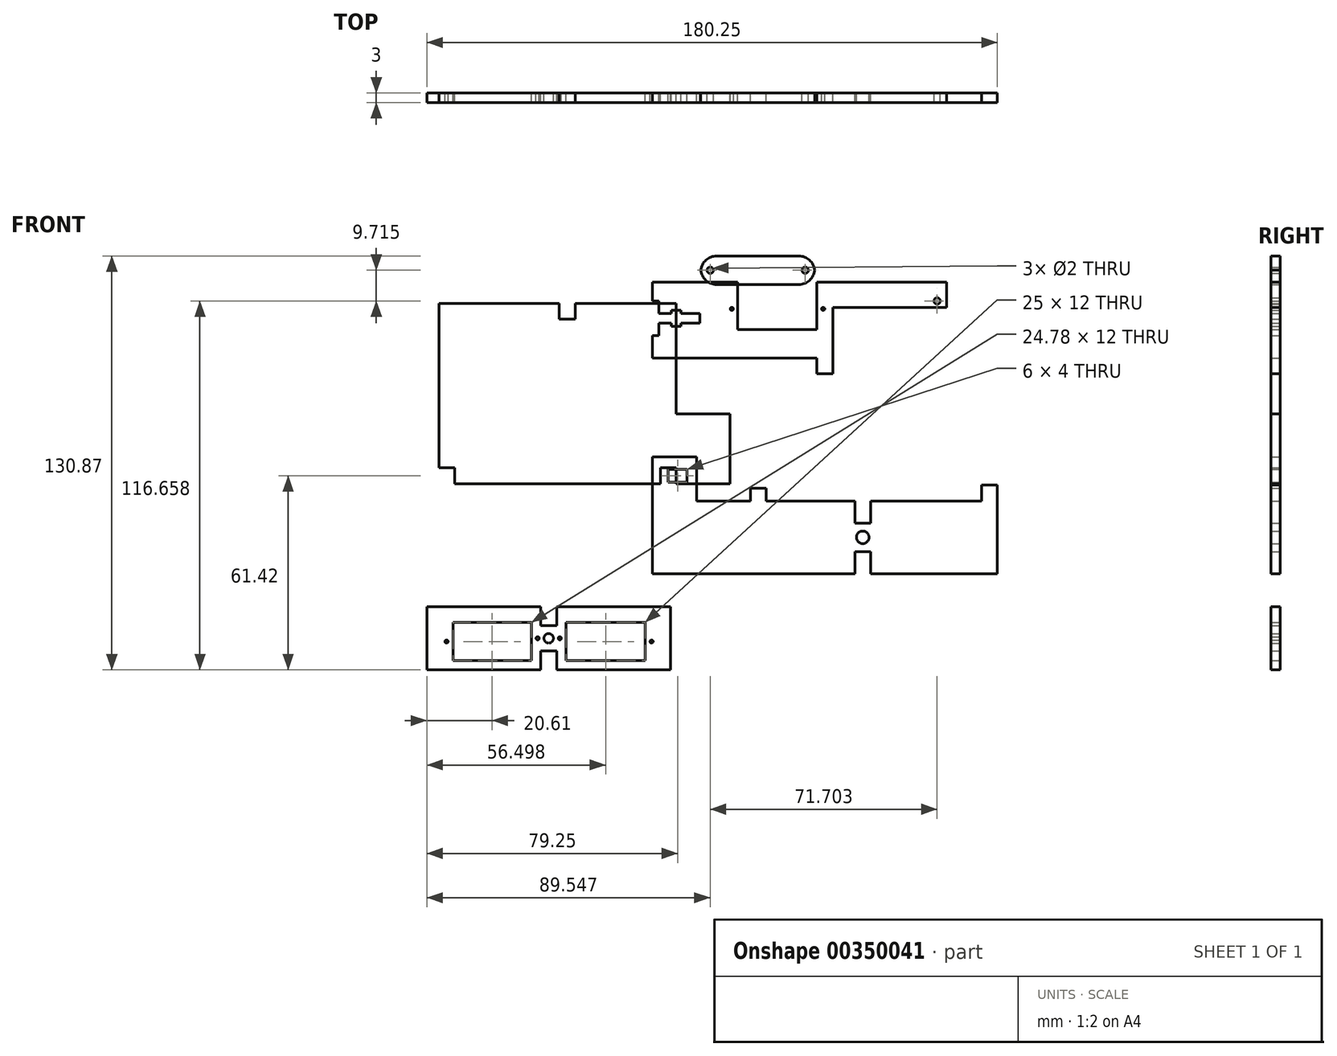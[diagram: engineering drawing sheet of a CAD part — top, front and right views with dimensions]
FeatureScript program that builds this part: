
annotation { "Feature Type Name" : "Feature", "Feature Type Description" : "" }
export const myFeature = defineFeature(function(context is Context, id is Id, definition is map)
    precondition{}
    {
        {
            var Q0;
            Q0=qCreatedBy(makeId("Front.planeOp"),FACE);
            var sketch = newSketch(context, id + "F0", { "sketchPlane" : qUnion([Q0])});
            skLineSegment(sketch, "E0", {"start": v(-67.42, 48.47) * mm, "end": v(-29.42, 48.47) * mm});
            skLineSegment(sketch, "E1", {"start": v(-29.42, 48.47) * mm, "end": v(-29.42, 43.47) * mm});
            skLineSegment(sketch, "E2", {"start": v(-29.42, 43.47) * mm, "end": v(-24.42, 43.47) * mm});
            skLineSegment(sketch, "E3", {"start": v(-24.42, 43.47) * mm, "end": v(-24.42, 48.47) * mm});
            skLineSegment(sketch, "E4", {"start": v(-24.42, 48.47) * mm, "end": v(7.58, 48.47) * mm});
            skLineSegment(sketch, "E5", {"start": v(7.58, 48.47) * mm, "end": v(7.58, 13.47) * mm});
            skLineSegment(sketch, "E6", {"start": v(7.58, 13.47) * mm, "end": v(24.58, 13.47) * mm});
            skLineSegment(sketch, "E7", {"start": v(24.58, 13.47) * mm, "end": v(24.58, -8.53) * mm});
            skLineSegment(sketch, "E8", {"start": v(24.58, -8.53) * mm, "end": v(7.58, -8.53) * mm});
            skLineSegment(sketch, "E9", {"start": v(7.58, -8.53) * mm, "end": v(7.58, -3.53) * mm});
            skLineSegment(sketch, "E10", {"start": v(7.58, -3.53) * mm, "end": v(2.58, -3.53) * mm});
            skLineSegment(sketch, "E11", {"start": v(2.58, -3.53) * mm, "end": v(2.58, -8.53) * mm});
            skLineSegment(sketch, "E12", {"start": v(2.58, -8.53) * mm, "end": v(-62.42, -8.53) * mm});
            skLineSegment(sketch, "E13", {"start": v(-62.42, -8.53) * mm, "end": v(-62.42, -3.53) * mm});
            skLineSegment(sketch, "E14", {"start": v(-62.42, -3.53) * mm, "end": v(-67.42, -3.53) * mm});
            skLineSegment(sketch, "E15", {"start": v(-67.42, 48.47) * mm, "end": v(-67.42, -3.53) * mm});
            skSolve(sketch);
        }
        {
            var Q0;
            Q0 = qSketchRegion(id + "F0", true);
            extrude(context, id + "F1", {"entities" : qUnion([Q0]), "depth" : 3 * mm});
        }
        {
            var Q0;
            Q0=qCreatedBy(makeId("Front.planeOp"),FACE);
            var sketch = newSketch(context, id + "F2", { "sketchPlane" : qUnion([Q0])});
            skLineSegment(sketch, "E16", {"start": v(0, 0) * mm, "end": v(14, 0) * mm});
            skLineSegment(sketch, "E17", {"start": v(14, 0) * mm, "end": v(14, -14) * mm});
            skLineSegment(sketch, "E18", {"start": v(14, -14) * mm, "end": v(31, -14) * mm});
            skLineSegment(sketch, "E19", {"start": v(31, -14) * mm, "end": v(31, -10) * mm});
            skLineSegment(sketch, "E20", {"start": v(31, -10) * mm, "end": v(36, -10) * mm});
            skLineSegment(sketch, "E21", {"start": v(36, -10) * mm, "end": v(36, -14) * mm});
            skLineSegment(sketch, "E22", {"start": v(36, -14) * mm, "end": v(64, -14) * mm});
            skLineSegment(sketch, "E23", {"start": v(64, -14) * mm, "end": v(64, -21) * mm});
            skLineSegment(sketch, "E24", {"start": v(64, -21) * mm, "end": v(69, -21) * mm});
            skLineSegment(sketch, "E25", {"start": v(69, -21) * mm, "end": v(69, -14) * mm});
            skLineSegment(sketch, "E26", {"start": v(69, -14) * mm, "end": v(104, -14) * mm});
            skLineSegment(sketch, "E27", {"start": v(104, -14) * mm, "end": v(104, -9) * mm});
            skLineSegment(sketch, "E28", {"start": v(104, -9) * mm, "end": v(109, -9) * mm});
            skLineSegment(sketch, "E29", {"start": v(109, -9) * mm, "end": v(109, -37) * mm});
            skLineSegment(sketch, "E30", {"start": v(109, -37) * mm, "end": v(69, -37) * mm});
            skLineSegment(sketch, "E31", {"start": v(69, -37) * mm, "end": v(69, -30) * mm});
            skLineSegment(sketch, "E32", {"start": v(69, -30) * mm, "end": v(64, -30) * mm});
            skLineSegment(sketch, "E33", {"start": v(64, -30) * mm, "end": v(64, -37) * mm});
            skLineSegment(sketch, "E34", {"start": v(64, -37) * mm, "end": v(0, -37) * mm});
            skLineSegment(sketch, "E35", {"start": v(0, -37) * mm, "end": v(0, 0) * mm});
            skCircle(sketch, "E36", {"center": v(66.5, -25.5) * mm, "radius": 2 * mm});
            skLineSegment(sketch, "E37.bottom", {"start": v(5, -4) * mm, "end": v(11, -4) * mm});
            skLineSegment(sketch, "E37.top", {"start": v(5, -8) * mm, "end": v(11, -8) * mm});
            skLineSegment(sketch, "E37.left", {"start": v(5, -4) * mm, "end": v(5, -8) * mm});
            skLineSegment(sketch, "E37.right", {"start": v(11, -4) * mm, "end": v(11, -8) * mm});
            skSolve(sketch);
        }
        {
            var Q0;
            Q0 = qSketchRegion(id + "F2", true);
            extrude(context, id + "F3", {"entities" : qUnion([Q0]), "depth" : 3 * mm});
        }
        {
            var Q0;
            Q0=qCreatedBy(makeId("Front.planeOp"),FACE);
            var sketch = newSketch(context, id + "F4", { "sketchPlane" : qUnion([Q0])});
            skLineSegment(sketch, "E38", {"start": v(-71.25, -67.42) * mm, "end": v(-35.25, -67.42) * mm});
            skLineSegment(sketch, "E39", {"start": v(-35.25, -67.42) * mm, "end": v(-35.25, -61.42) * mm});
            skLineSegment(sketch, "E40", {"start": v(-35.25, -61.42) * mm, "end": v(-30.25, -61.42) * mm});
            skLineSegment(sketch, "E41", {"start": v(-30.25, -61.42) * mm, "end": v(-30.25, -67.42) * mm});
            skLineSegment(sketch, "E42", {"start": v(-30.25, -67.42) * mm, "end": v(5.75, -67.42) * mm});
            skLineSegment(sketch, "E43", {"start": v(5.75, -67.42) * mm, "end": v(5.75, -47.42) * mm});
            skLineSegment(sketch, "E44", {"start": v(5.75, -47.42) * mm, "end": v(-30.25, -47.42) * mm});
            skLineSegment(sketch, "E45", {"start": v(-30.25, -47.42) * mm, "end": v(-30.25, -53.42) * mm});
            skLineSegment(sketch, "E46", {"start": v(-30.25, -53.42) * mm, "end": v(-35.25, -53.42) * mm});
            skLineSegment(sketch, "E47", {"start": v(-35.25, -53.42) * mm, "end": v(-35.25, -47.42) * mm});
            skLineSegment(sketch, "E48", {"start": v(-35.25, -47.42) * mm, "end": v(-71.25, -47.42) * mm});
            skLineSegment(sketch, "E49", {"start": v(-71.25, -47.42) * mm, "end": v(-71.25, -67.42) * mm});
            skLineSegment(sketch, "E50.bottom", {"start": v(-63.03, -52.42) * mm, "end": v(-38.25, -52.42) * mm});
            skLineSegment(sketch, "E50.top", {"start": v(-63.03, -64.42) * mm, "end": v(-38.25, -64.42) * mm});
            skLineSegment(sketch, "E50.left", {"start": v(-63.03, -52.42) * mm, "end": v(-63.03, -64.42) * mm});
            skLineSegment(sketch, "E50.right", {"start": v(-38.25, -52.42) * mm, "end": v(-38.25, -64.42) * mm});
            skLineSegment(sketch, "E51.MirrorCS", {"start": v(-2.25, -52.42) * mm, "end": v(-27.25, -52.42) * mm});
            skLineSegment(sketch, "E52.MirrorCS", {"start": v(-27.25, -52.42) * mm, "end": v(-27.25, -64.42) * mm});
            skLineSegment(sketch, "E53.MirrorCS", {"start": v(-2.25, -64.42) * mm, "end": v(-27.25, -64.42) * mm});
            skLineSegment(sketch, "E54.MirrorCS", {"start": v(-2.25, -52.42) * mm, "end": v(-2.25, -64.42) * mm});
            skCircle(sketch, "E55", {"center": v(-36.25, -57.42) * mm, "radius": 0.5 * mm});
            skCircle(sketch, "E56.MirrorC", {"center": v(-29.25, -57.42) * mm, "radius": 0.5 * mm});
            skCircle(sketch, "E57", {"center": v(-32.75, -57.42) * mm, "radius": 1.5 * mm});
            skCircle(sketch, "E58", {"center": v(-65.03, -58.42) * mm, "radius": 0.5 * mm});
            skCircle(sketch, "E59", {"center": v(-0.25, -58.42) * mm, "radius": 0.5 * mm});
            skSolve(sketch);
        }
        {
            var Q0;
            Q0 = qSketchRegion(id + "F4", true);
            extrude(context, id + "F5", {"entities" : qUnion([Q0]), "depth" : 3 * mm});
        }
        {
            var Q0;
            Q0=qCreatedBy(makeId("Front.planeOp"),FACE);
            var sketch = newSketch(context, id + "F6", { "sketchPlane" : qUnion([Q0])});
            skLineSegment(sketch, "E60", {"start": v(15.3, 63.45) * mm, "end": v(51.3, 63.45) * mm});
            skLineSegment(sketch, "E61", {"start": v(51.3, 63.45) * mm, "end": v(51.3, 54.45) * mm});
            skLineSegment(sketch, "E62", {"start": v(51.3, 54.45) * mm, "end": v(15.3, 54.45) * mm});
            skLineSegment(sketch, "E63", {"start": v(15.3, 54.45) * mm, "end": v(15.3, 63.45) * mm});
            skCircle(sketch, "E64", {"center": v(18.3, 58.95) * mm, "radius": 1 * mm});
            skCircle(sketch, "E65.MirrorC", {"center": v(48.3, 58.95) * mm, "radius": 1 * mm});
            skSolve(sketch);
        }
        {
            var Q0;
            Q0 = qSketchRegion(id + "F6", true);
            extrude(context, id + "F7", {"entities" : qUnion([Q0]), "depth" : 3 * mm});
        }
        {
            var Q0;
            Q0=makeQuery(id+"F7.opExtrude","SWEPT_EDGE",EDGE,{"disambiguationData":[OSD([sQuery(id+"F6.wireOp",EDGE,"E60"),sQuery(id+"F6.wireOp",EDGE,"E63")])]});
            var Q1;
            Q1=makeQuery(id+"F7.opExtrude","SWEPT_EDGE",EDGE,{"disambiguationData":[OSD([sQuery(id+"F6.wireOp",EDGE,"E62"),sQuery(id+"F6.wireOp",EDGE,"E63")])]});
            var Q2;
            Q2=makeQuery(id+"F7.opExtrude","SWEPT_EDGE",EDGE,{"disambiguationData":[OSD([sQuery(id+"F6.wireOp",EDGE,"E60"),sQuery(id+"F6.wireOp",EDGE,"E61")])]});
            var Q3;
            Q3=makeQuery(id+"F7.opExtrude","SWEPT_EDGE",EDGE,{"disambiguationData":[OSD([sQuery(id+"F6.wireOp",EDGE,"E61"),sQuery(id+"F6.wireOp",EDGE,"E62")])]});
            fillet(context, id + "F8", {"entities" : qUnion([Q0, Q1, Q2, Q3]), "radius" : 5 * mm, "tangentPropagation" : true, "allowEdgeOverflow" : false});
        }
        {
            var Q0;
            Q0=qCreatedBy(makeId("Front.planeOp"),FACE);
            var sketch = newSketch(context, id + "F9", { "sketchPlane" : qUnion([Q0])});
            skLineSegment(sketch, "E66", {"start": v(0, 55.24) * mm, "end": v(27, 55.24) * mm});
            skLineSegment(sketch, "E67", {"start": v(27, 55.24) * mm, "end": v(27, 40.24) * mm});
            skLineSegment(sketch, "E68", {"start": v(27, 40.24) * mm, "end": v(52, 40.24) * mm});
            skLineSegment(sketch, "E69", {"start": v(52, 40.24) * mm, "end": v(52, 55.24) * mm});
            skLineSegment(sketch, "E70", {"start": v(52, 55.24) * mm, "end": v(93, 55.24) * mm});
            skLineSegment(sketch, "E71", {"start": v(93, 55.24) * mm, "end": v(93, 47.24) * mm});
            skLineSegment(sketch, "E72", {"start": v(93, 47.24) * mm, "end": v(57, 47.24) * mm});
            skLineSegment(sketch, "E73", {"start": v(57, 47.24) * mm, "end": v(57, 26.24) * mm});
            skLineSegment(sketch, "E74", {"start": v(57, 26.24) * mm, "end": v(52, 26.24) * mm});
            skLineSegment(sketch, "E75", {"start": v(52, 26.24) * mm, "end": v(52, 31.24) * mm});
            skLineSegment(sketch, "E76", {"start": v(52, 31.24) * mm, "end": v(0, 31.24) * mm});
            skLineSegment(sketch, "E77", {"start": v(0, 55.24) * mm, "end": v(0, 49.24) * mm});
            skLineSegment(sketch, "E78", {"start": v(0, 49.24) * mm, "end": v(2, 49.24) * mm});
            skLineSegment(sketch, "E79", {"start": v(2, 49.24) * mm, "end": v(2, 45.24) * mm});
            skLineSegment(sketch, "E80", {"start": v(2, 45.24) * mm, "end": v(6, 45.24) * mm});
            skLineSegment(sketch, "E81", {"start": v(6, 45.24) * mm, "end": v(6, 46.24) * mm});
            skLineSegment(sketch, "E82", {"start": v(6, 46.24) * mm, "end": v(9, 46.24) * mm});
            skLineSegment(sketch, "E83", {"start": v(9, 46.24) * mm, "end": v(9, 45.24) * mm});
            skLineSegment(sketch, "E84", {"start": v(9, 45.24) * mm, "end": v(15, 45.24) * mm});
            skLineSegment(sketch, "E85", {"start": v(15, 45.24) * mm, "end": v(15, 42.24) * mm});
            skLineSegment(sketch, "E86", {"start": v(15, 42.24) * mm, "end": v(9, 42.24) * mm});
            skLineSegment(sketch, "E87", {"start": v(9, 42.24) * mm, "end": v(9, 41.24) * mm});
            skLineSegment(sketch, "E88", {"start": v(9, 41.24) * mm, "end": v(6, 41.24) * mm});
            skLineSegment(sketch, "E89", {"start": v(6, 41.24) * mm, "end": v(6, 42.24) * mm});
            skLineSegment(sketch, "E90", {"start": v(6, 42.24) * mm, "end": v(2, 42.24) * mm});
            skLineSegment(sketch, "E91", {"start": v(2, 42.24) * mm, "end": v(2, 38.24) * mm});
            skLineSegment(sketch, "E92", {"start": v(2, 38.24) * mm, "end": v(0, 38.24) * mm});
            skLineSegment(sketch, "E93", {"start": v(0, 38.24) * mm, "end": v(0, 31.24) * mm});
            skCircle(sketch, "E94", {"center": v(25.12, 46.74) * mm, "radius": 0.5 * mm});
            skCircle(sketch, "E95", {"center": v(54, 46.74) * mm, "radius": 0.5 * mm});
            skCircle(sketch, "E96", {"center": v(90, 49.24) * mm, "radius": 1 * mm});
            skSolve(sketch);
        }
        {
            var Q0;
            Q0 = qSketchRegion(id + "F9", true);
            extrude(context, id + "F10", {"entities" : qUnion([Q0]), "depth" : 3 * mm});
        }
    });
